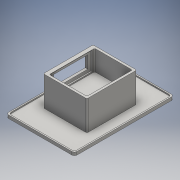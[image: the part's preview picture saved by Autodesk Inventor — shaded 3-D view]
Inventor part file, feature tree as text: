
AUTODESK INVENTOR PART (.ipt)
format: ipt  version: 2016 (Build 200138000, 138)  size: 201,728 bytes
history: native  units: mm
features: extrude x6, sketch x6
ambient origin geometry x8: Origin, YZ Plane, XZ Plane, XY Plane, X Axis, Y Axis, Z Axis, Center Point
bodies: Solid1 (feature_tree)
feature tree (12):
  extrude  "xyAttach"  Depth=159.5mm
  extrude  "spillExtrusion"  Depth=79.75mm
  extrude  "chamberWallExtrusion"  Depth=3.0mm TaperAngle=0.0deg
  extrude  "chamberInteriorExtrusion"  Depth=4.0mm
  extrude  "rectCoverSlipMountExtrusion"  Depth=2.0mm
  extrude  "rectCoverSlipWindow"  Depth=2.0mm
  sketch  "Sketch1"  dims[d0=109.5mm d1=159.5mm]
  sketch  "Sketch2"  dims[d2=54.75mm d3=79.75mm]
  sketch  "Sketch3"  dims[d4=4.0mm d5=3.0mm d6=0.0mm]
  sketch  "Sketch4"  dims[d7=4.0mm d8=4.0mm]
  sketch  "Sketch5"  dims[d9=2.0mm d10=2.0mm]
  sketch  "Sketch6"  dims[d11=2.0mm d12=2.0mm d13=2.0mm d14=0.0mm d15=70.0mm d16=35.0mm d17=80.0mm d18=40.0mm d19=2.0mm d20=47.5mm d21=0.0mm d22=2.0mm d23=3.5mm d24=3.5mm d25=3.5mm d26=6.0mm d27=32.5mm d28=0.0mm d29=65.0mm d30=30.0mm d31=32.5mm d32=45.0mm d33=2.0mm d34=0.0mm d35=55.0mm d36=20.0mm d37=40.0mm d38=27.5mm d39=2.0mm d40=0.0mm]
